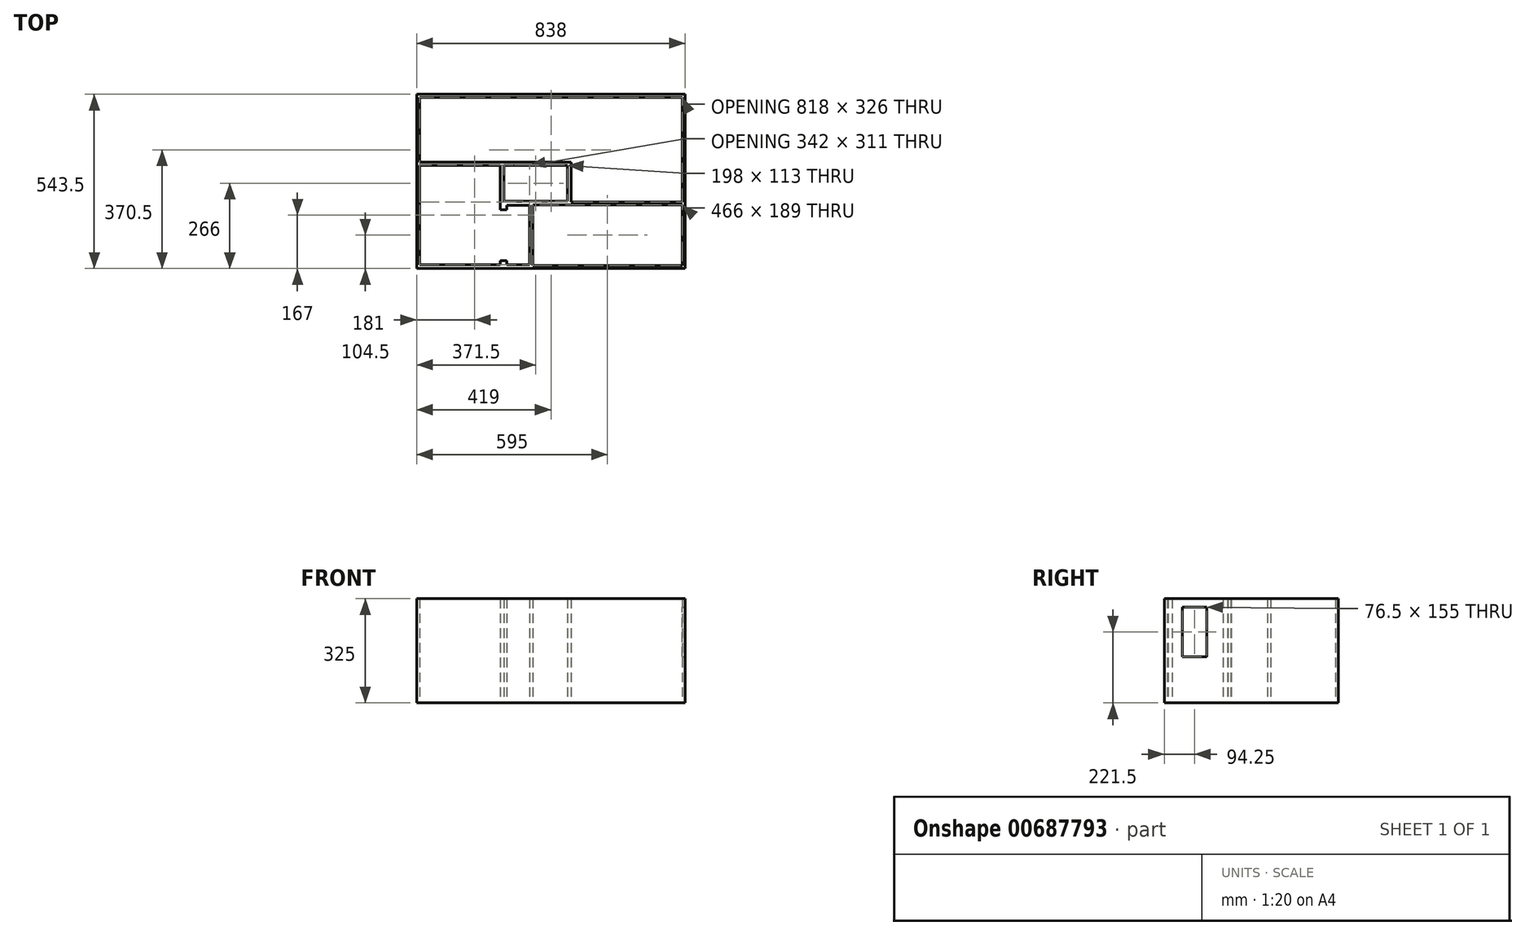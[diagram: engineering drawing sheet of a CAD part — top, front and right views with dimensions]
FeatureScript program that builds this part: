
annotation { "Feature Type Name" : "Feature", "Feature Type Description" : "" }
export const myFeature = defineFeature(function(context is Context, id is Id, definition is map)
    precondition{}
    {
        {
            var Q0;
            Q0=qCreatedBy(makeId("Top.planeOp"),FACE);
            var sketch = newSketch(context, id + "F0", { "sketchPlane" : qUnion([Q0])});
            skLineSegment(sketch, "E0.bottom", {"start": v(0, 0) * mm, "end": v(466, 0) * mm});
            skLineSegment(sketch, "E0.top", {"start": v(0, -186) * mm, "end": v(466, -186) * mm});
            skLineSegment(sketch, "E0.left", {"start": v(0, 0) * mm, "end": v(0, -186) * mm});
            skLineSegment(sketch, "E0.right", {"start": v(466, 0) * mm, "end": v(466, -186) * mm});
            skLineSegment(sketch, "E1.top", {"start": v(0, 1.5) * mm, "end": v(466, 1.5) * mm});
            skLineSegment(sketch, "E1.left", {"start": v(0, 0) * mm, "end": v(0, 1.5) * mm});
            skLineSegment(sketch, "E1.right", {"start": v(466, 0) * mm, "end": v(466, 1.5) * mm});
            skLineSegment(sketch, "E2.top", {"start": v(0, -187.5) * mm, "end": v(466, -187.5) * mm});
            skLineSegment(sketch, "E2.left", {"start": v(0, -186) * mm, "end": v(0, -187.5) * mm});
            skLineSegment(sketch, "E2.right", {"start": v(466, -186) * mm, "end": v(466, -187.5) * mm});
            skLineSegment(sketch, "E3.bottom", {"start": v(466, 10) * mm, "end": v(120, 10) * mm});
            skLineSegment(sketch, "E3.top", {"start": v(466, 336) * mm, "end": v(120, 336) * mm});
            skLineSegment(sketch, "E3.left", {"start": v(466, 10) * mm, "end": v(466, 336) * mm});
            skLineSegment(sketch, "E3.right", {"start": v(120, 10) * mm, "end": v(120, 336) * mm});
            skLineSegment(sketch, "E4.bottom", {"start": v(120, 336) * mm, "end": v(466, 336) * mm});
            skLineSegment(sketch, "E4.top", {"start": v(120, 276) * mm, "end": v(466, 276) * mm});
            skLineSegment(sketch, "E4.left", {"start": v(120, 336) * mm, "end": v(120, 276) * mm});
            skLineSegment(sketch, "E4.right", {"start": v(466, 336) * mm, "end": v(466, 276) * mm});
            skLineSegment(sketch, "E5.bottom", {"start": v(-10, 0) * mm, "end": v(-81, 0) * mm});
            skLineSegment(sketch, "E5.top", {"start": v(-10, -186) * mm, "end": v(-81, -186) * mm});
            skLineSegment(sketch, "E5.left", {"start": v(-10, 0) * mm, "end": v(-10, -186) * mm});
            skLineSegment(sketch, "E5.right", {"start": v(-81, 0) * mm, "end": v(-81, -186) * mm});
            skLineSegment(sketch, "E6.bottom", {"start": v(-101, -186) * mm, "end": v(-352, -186) * mm});
            skLineSegment(sketch, "E6.top", {"start": v(-101, 125) * mm, "end": v(-352, 125) * mm});
            skLineSegment(sketch, "E6.left", {"start": v(-101, -186) * mm, "end": v(-101, 125) * mm});
            skLineSegment(sketch, "E6.right", {"start": v(-352, -186) * mm, "end": v(-352, 125) * mm});
            skLineSegment(sketch, "E7.bottom", {"start": v(-278.95, -186) * mm, "end": v(-148.95, -186) * mm});
            skLineSegment(sketch, "E7.top", {"start": v(-278.95, -143) * mm, "end": v(-148.95, -143) * mm});
            skLineSegment(sketch, "E7.left", {"start": v(-278.95, -186) * mm, "end": v(-278.95, -143) * mm});
            skLineSegment(sketch, "E7.right", {"start": v(-148.95, -186) * mm, "end": v(-148.95, -143) * mm});
            skLineSegment(sketch, "E8.bottom", {"start": v(-256.09, -143) * mm, "end": v(-167.96, -143) * mm});
            skLineSegment(sketch, "E8.top", {"start": v(-256.09, -129) * mm, "end": v(-167.96, -129) * mm});
            skLineSegment(sketch, "E8.left", {"start": v(-256.09, -143) * mm, "end": v(-256.09, -129) * mm});
            skLineSegment(sketch, "E8.right", {"start": v(-167.96, -143) * mm, "end": v(-167.96, -129) * mm});
            skLineSegment(sketch, "E9.bottom", {"start": v(-101, -13.5) * mm, "end": v(-81, -13.5) * mm});
            skLineSegment(sketch, "E9.top", {"start": v(-101, -172.5) * mm, "end": v(-81, -172.5) * mm});
            skLineSegment(sketch, "E9.left", {"start": v(-101, -13.5) * mm, "end": v(-101, -172.5) * mm});
            skLineSegment(sketch, "E9.right", {"start": v(-81, -13.5) * mm, "end": v(-81, -172.5) * mm});
            skLineSegment(sketch, "E10", {"start": v(-101, -93) * mm, "end": v(-10, -93) * mm, "construction": true});
            skLineSegment(sketch, "E11.bottom", {"start": v(-352, 135) * mm, "end": v(120, 135) * mm});
            skLineSegment(sketch, "E11.top", {"start": v(-352, 225) * mm, "end": v(120, 225) * mm});
            skLineSegment(sketch, "E11.left", {"start": v(-352, 135) * mm, "end": v(-352, 225) * mm});
            skLineSegment(sketch, "E11.right", {"start": v(120, 135) * mm, "end": v(120, 225) * mm});
            skLineSegment(sketch, "E12.bottom", {"start": v(-89.5, 125) * mm, "end": v(108.5, 125) * mm});
            skLineSegment(sketch, "E12.top", {"start": v(-89.5, 12) * mm, "end": v(108.5, 12) * mm});
            skLineSegment(sketch, "E12.left", {"start": v(-89.5, 125) * mm, "end": v(-89.5, 12) * mm});
            skLineSegment(sketch, "E12.right", {"start": v(108.5, 125) * mm, "end": v(108.5, 12) * mm});
            skLineSegment(sketch, "E13", {"start": v(-101, 125) * mm, "end": v(-89.5, 125) * mm, "construction": true});
            skLineSegment(sketch, "E14", {"start": v(108.5, 125) * mm, "end": v(120, 125) * mm, "construction": true});
            skLineSegment(sketch, "E15", {"start": v(-0.5, 125) * mm, "end": v(-0.5, 12) * mm});
            skLineSegment(sketch, "E16.bottom", {"start": v(110, 336) * mm, "end": v(13, 336) * mm});
            skLineSegment(sketch, "E16.top", {"start": v(110, 241) * mm, "end": v(13, 241) * mm});
            skLineSegment(sketch, "E16.left", {"start": v(110, 336) * mm, "end": v(110, 241) * mm});
            skLineSegment(sketch, "E16.right", {"start": v(13, 336) * mm, "end": v(13, 241) * mm});
            skLineSegment(sketch, "E17.bottom", {"start": v(0, 336) * mm, "end": v(-89.5, 336) * mm});
            skLineSegment(sketch, "E17.top", {"start": v(0, 241) * mm, "end": v(-89.5, 241) * mm});
            skLineSegment(sketch, "E17.left", {"start": v(0, 336) * mm, "end": v(0, 241) * mm});
            skLineSegment(sketch, "E17.right", {"start": v(-89.5, 336) * mm, "end": v(-89.5, 241) * mm});
            skLineSegment(sketch, "E18.bottom", {"start": v(-101, 241) * mm, "end": v(-352, 241) * mm});
            skLineSegment(sketch, "E18.top", {"start": v(-101, 336) * mm, "end": v(-352, 336) * mm});
            skLineSegment(sketch, "E18.left", {"start": v(-101, 241) * mm, "end": v(-101, 336) * mm});
            skLineSegment(sketch, "E18.right", {"start": v(-352, 241) * mm, "end": v(-352, 336) * mm});
            skLineSegment(sketch, "E19", {"start": v(-101, 336) * mm, "end": v(-89.5, 336) * mm});
            skLineSegment(sketch, "E20", {"start": v(0, 336) * mm, "end": v(13, 336) * mm});
            skLineSegment(sketch, "E21", {"start": v(110, 336) * mm, "end": v(120, 336) * mm});
            skLineSegment(sketch, "E22", {"start": v(-352, 241) * mm, "end": v(-352, 225) * mm});
            skLineSegment(sketch, "E23", {"start": v(-352, 135) * mm, "end": v(-352, 125) * mm});
            skLineSegment(sketch, "E24", {"start": v(-101, -186) * mm, "end": v(-81, -186) * mm});
            skLineSegment(sketch, "E25", {"start": v(-10, -186) * mm, "end": v(0, -186) * mm});
            skLineSegment(sketch, "E26", {"start": v(466, 0) * mm, "end": v(466, 10) * mm});
            skLineSegment(sketch, "E27.bottom", {"start": v(-362, 346) * mm, "end": v(476, 346) * mm});
            skLineSegment(sketch, "E27.top", {"start": v(-362, -197.5) * mm, "end": v(476, -197.5) * mm});
            skLineSegment(sketch, "E27.left", {"start": v(-362, 346) * mm, "end": v(-362, -197.5) * mm});
            skLineSegment(sketch, "E27.right", {"start": v(476, 346) * mm, "end": v(476, -197.5) * mm});
            skSolve(sketch);
        }
        {
            var Q0;
            {var subQ0=sQuery(id+"F0.wireOp",EDGE,"E4.left");Q0=makeQuery(id+"F0.imprint","IMPRINT",FACE,{"disambiguationData":[TD([[makeQuery(id+"F0.imprint","IMPRINT",EDGE,{"derivedFrom":subQ0}),-1.0]])]});}
            var Q1;
            Q1=makeQuery(id+"F0.imprint","IMPRINT",FACE,{"disambiguationData":[TD([[makeQuery(id+"F0.imprint","IMPRINT",EDGE,{"derivedFrom":sQuery(id+"F0.wireOp",EDGE,"E0.left")}),-1.0]])]});
            var Q2;
            {var subQ2=sQuery(id+"F0.wireOp",EDGE,"E9.top");Q2=makeQuery(id+"F0.imprint","IMPRINT",FACE,{"disambiguationData":[TD([[makeQuery(id+"F0.imprint","IMPRINT",EDGE,{"derivedFrom":subQ2}),-1.0]])]});}
            var Q3;
            {var subQ2=sQuery(id+"F0.wireOp",EDGE,"E0.right");Q3=makeQuery(id+"F0.imprint","IMPRINT",FACE,{"disambiguationData":[TD([[makeQuery(id+"F0.imprint","IMPRINT",EDGE,{"derivedFrom":subQ2}),1.0]])]});}
            extrude(context, id + "F1", {"entities" : qUnion([Q0, Q1, Q2, Q3]), "depth" : 325 * mm, "offsetDistance" : 25 * mm});
        }
        {
            var Q0;
            Q0=makeQuery(id+"F1.opExtrude","SWEPT_FACE",FACE,{"disambiguationData":[OSD([sQuery(id+"F0.wireOp",EDGE,"E27.right")])]});
            var sketch = newSketch(context, id + "F2", { "sketchPlane" : qUnion([Q0])});
            skLineSegment(sketch, "E28.bottom", {"start": v(-141.5, 299) * mm, "end": v(-65, 299) * mm});
            skLineSegment(sketch, "E28.top", {"start": v(-141.5, 144) * mm, "end": v(-65, 144) * mm});
            skLineSegment(sketch, "E28.left", {"start": v(-141.5, 299) * mm, "end": v(-141.5, 144) * mm});
            skLineSegment(sketch, "E28.right", {"start": v(-65, 299) * mm, "end": v(-65, 144) * mm});
            skSolve(sketch);
        }
        {
            var Q0;
            Q0=makeQuery(id+"F2.imprint","IMPRINT",FACE,{"disambiguationData":[TD([[makeQuery(id+"F2.imprint","IMPRINT",EDGE,{"derivedFrom":sQuery(id+"F2.wireOp",EDGE,"E28.bottom")}),-1.0]])]});
            extrude(context, id + "F3", {"entities" : qUnion([Q0]), "operationType" : NewBodyOperationType.REMOVE, "oppositeDirection" : true, "depth" : 25 * mm, "offsetDistance" : 25 * mm});
        }
    });
